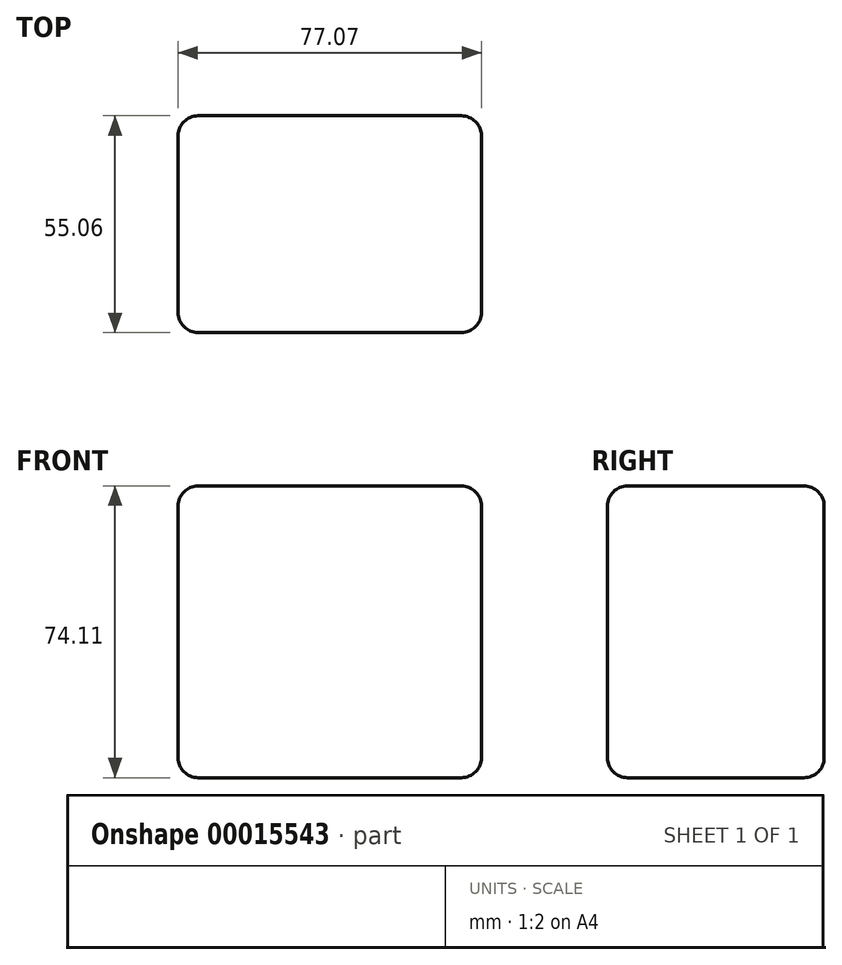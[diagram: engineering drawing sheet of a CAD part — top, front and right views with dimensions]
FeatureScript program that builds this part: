
annotation { "Feature Type Name" : "Feature", "Feature Type Description" : "" }
export const myFeature = defineFeature(function(context is Context, id is Id, definition is map)
    precondition{}
    {
        {
            var Q0;
            Q0=qCreatedBy(makeId("Front.planeOp"),FACE);
            var sketch = newSketch(context, id + "F0", { "sketchPlane" : qUnion([Q0])});
            skLineSegment(sketch, "E0.bottom", {"start": v(0, 0) * mm, "end": v(77.07, 0) * mm});
            skLineSegment(sketch, "E0.top", {"start": v(0, 74.11) * mm, "end": v(77.07, 74.11) * mm});
            skLineSegment(sketch, "E0.left", {"start": v(0, 0) * mm, "end": v(0, 74.11) * mm});
            skLineSegment(sketch, "E0.right", {"start": v(77.07, 0) * mm, "end": v(77.07, 74.11) * mm});
            skSolve(sketch);
        }
        {
            var Q0;
            Q0=makeQuery(id+"F0.imprint","IMPRINT",FACE,{"disambiguationData":[TD([[makeQuery(id+"F0.imprint","IMPRINT",EDGE,{"derivedFrom":sQuery(id+"F0.wireOp",EDGE,"E0.bottom")}),1.0]])]});
            extrude(context, id + "F1", {"entities" : qUnion([Q0]), "depth" : 55.06 * mm});
        }
        {
            var Q0;
            Q0=makeQuery(id+"F1.opExtrude","SWEPT_EDGE",EDGE,{"disambiguationData":[OSD([sQuery(id+"F0.wireOp",EDGE,"E0.top"),sQuery(id+"F0.wireOp",EDGE,"E0.right")])]});
            var Q1;
            Q1=makeQuery(id+"F1.opExtrude","SWEPT_EDGE",EDGE,{"disambiguationData":[OSD([sQuery(id+"F0.wireOp",EDGE,"E0.top"),sQuery(id+"F0.wireOp",EDGE,"E0.left")])]});
            var Q2;
            Q2=makeQuery(id+"F1.opExtrude","CAP_FACE",FACE,{"disambiguationData":[OSD([sQuery(id+"F0.wireOp",EDGE,"E0.bottom"),sQuery(id+"F0.wireOp",EDGE,"E0.top"),sQuery(id+"F0.wireOp",EDGE,"E0.left"),sQuery(id+"F0.wireOp",EDGE,"E0.right")])],"isStart":false});
            var Q3;
            Q3=makeQuery(id+"F1.opExtrude","CAP_EDGE",EDGE,{"disambiguationData":[OSD([sQuery(id+"F0.wireOp",EDGE,"E0.top")])],"isStart":true});
            var Q4;
            Q4=makeQuery(id+"F1.opExtrude","CAP_EDGE",EDGE,{"disambiguationData":[OSD([sQuery(id+"F0.wireOp",EDGE,"E0.right")])],"isStart":false});
            var Q5;
            Q5=makeQuery(id+"F1.opExtrude","CAP_EDGE",EDGE,{"disambiguationData":[OSD([sQuery(id+"F0.wireOp",EDGE,"E0.right")])],"isStart":true});
            var Q6;
            Q6=makeQuery(id+"F1.opExtrude","CAP_EDGE",EDGE,{"disambiguationData":[OSD([sQuery(id+"F0.wireOp",EDGE,"E0.left")])],"isStart":false});
            var Q7;
            Q7=makeQuery(id+"F1.opExtrude","SWEPT_FACE",FACE,{"disambiguationData":[OSD([sQuery(id+"F0.wireOp",EDGE,"E0.left")])]});
            fillet(context, id + "F2", {"entities" : qUnion([Q0, Q1, Q2, Q3, Q4, Q5, Q6, Q7]), "radius" : 5.08 * mm, "tangentPropagation" : true, "allowEdgeOverflow" : false});
        }
        {
            var Q0;
            Q0=makeQuery(id+"F1.opExtrude","SWEPT_FACE",FACE,{"disambiguationData":[OSD([sQuery(id+"F0.wireOp",EDGE,"E0.bottom")])]});
            var Q1;
            Q1=makeQuery(id+"F1.opExtrude","SWEPT_EDGE",EDGE,{"disambiguationData":[OSD([sQuery(id+"F0.wireOp",EDGE,"E0.bottom"),sQuery(id+"F0.wireOp",EDGE,"E0.right")])]});
            var Q2;
            {var subQ0=sQuery(id+"F0.wireOp",EDGE,"E0.bottom");Q2=makeQuery(id+"F2.opFillet","BLEND_EDGE",EDGE,{"blendedFrom":[makeQuery(id+"F1.opExtrude","CAP_EDGE",EDGE,{"disambiguationData":[OSD([subQ0])],"isStart":false}),makeQuery(id+"F1.opExtrude","CAP_FACE",FACE,{"disambiguationData":[OSD([subQ0,sQuery(id+"F0.wireOp",EDGE,"E0.top"),sQuery(id+"F0.wireOp",EDGE,"E0.left"),sQuery(id+"F0.wireOp",EDGE,"E0.right")])],"isStart":false})],"blendedInto":[makeQuery(id+"F1.opExtrude","CAP_FACE",FACE,{"disambiguationData":[OSD([subQ0,sQuery(id+"F0.wireOp",EDGE,"E0.top"),sQuery(id+"F0.wireOp",EDGE,"E0.left"),sQuery(id+"F0.wireOp",EDGE,"E0.right")])],"isStart":false})]});}
            var Q3;
            Q3=makeQuery(id+"F1.opExtrude","CAP_EDGE",EDGE,{"disambiguationData":[OSD([sQuery(id+"F0.wireOp",EDGE,"E0.bottom")])],"isStart":true});
            var Q4;
            {var subQ0=sQuery(id+"F0.wireOp",EDGE,"E0.bottom");Q4=makeQuery(id+"F2.opFillet","BLEND_EDGE",EDGE,{"blendedFrom":[makeQuery(id+"F1.opExtrude","SWEPT_EDGE",EDGE,{"disambiguationData":[OSD([subQ0,sQuery(id+"F0.wireOp",EDGE,"E0.left")])]}),makeQuery(id+"F1.opExtrude","SWEPT_FACE",FACE,{"disambiguationData":[OSD([subQ0])]})],"blendedInto":[makeQuery(id+"F1.opExtrude","SWEPT_FACE",FACE,{"disambiguationData":[OSD([subQ0])]})]});}
            fillet(context, id + "F3", {"entities" : qUnion([Q0, Q1, Q2, Q3, Q4]), "radius" : 5.08 * mm, "tangentPropagation" : true, "allowEdgeOverflow" : false});
        }
    });
